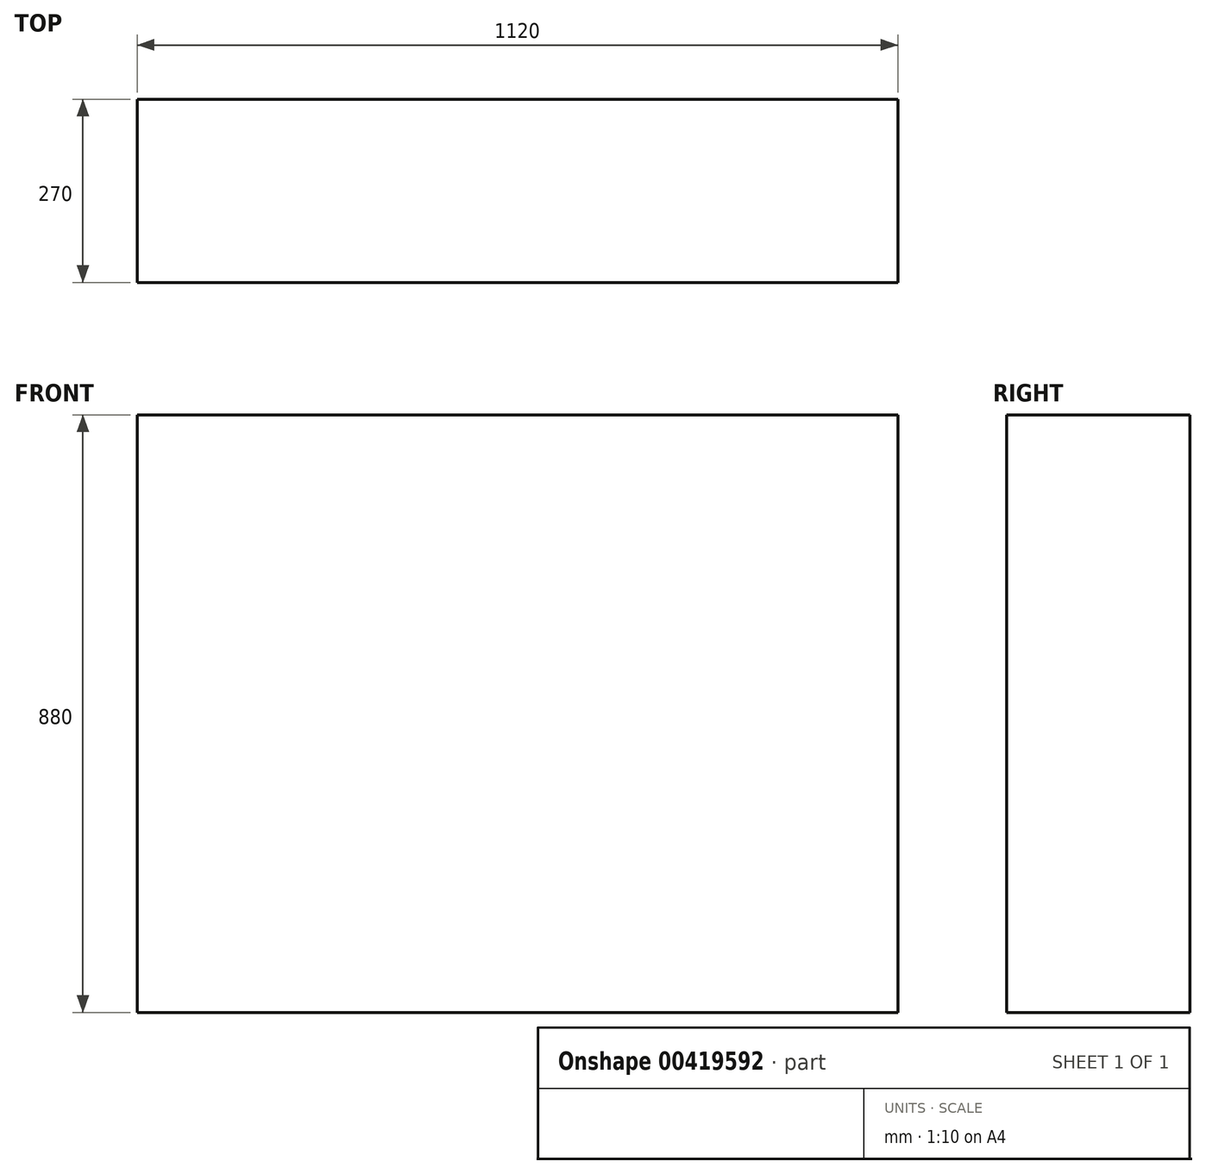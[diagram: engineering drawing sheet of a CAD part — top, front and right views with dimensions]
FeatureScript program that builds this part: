
annotation { "Feature Type Name" : "Feature", "Feature Type Description" : "" }
export const myFeature = defineFeature(function(context is Context, id is Id, definition is map)
    precondition{}
    {
        {
            var Q0;
            Q0=qCreatedBy(makeId("Top.planeOp"),FACE);
            var sketch = newSketch(context, id + "F0", { "sketchPlane" : qUnion([Q0])});
            skLineSegment(sketch, "E0.bottom", {"start": v(-1038.4, 228.76) * mm, "end": v(81.6, 228.76) * mm});
            skLineSegment(sketch, "E0.top", {"start": v(-1038.4, -41.24) * mm, "end": v(81.6, -41.24) * mm});
            skLineSegment(sketch, "E0.left", {"start": v(-1038.4, 228.76) * mm, "end": v(-1038.4, -41.24) * mm});
            skLineSegment(sketch, "E0.right", {"start": v(81.6, 228.76) * mm, "end": v(81.6, -41.24) * mm});
            skSolve(sketch);
        }
        {
            var Q0;
            Q0=makeQuery(id+"F0.imprint","IMPRINT",FACE,{"disambiguationData":[TD([[makeQuery(id+"F0.imprint","IMPRINT",EDGE,{"derivedFrom":sQuery(id+"F0.wireOp",EDGE,"E0.bottom")}),-1.0]])]});
            extrude(context, id + "F1", {"entities" : qUnion([Q0]), "depth" : 880 * mm});
        }
    });
